# Revit family: QF_GIORIK_MR4_MR42_MDR42
name_source: partatom
category: Specialty Equipment
revit_build: Autodesk Revit 2014 (Build: 20140709_2115(x64)
units: mm (PartAtom-declared; Revit-internal decimal feet)

## types (6) — shared parameters
Apparent Power = 6300 VA
Assembly Code = E1090320
Cold Water Connection Height = 56 mm  [stored 0.183727 ft]
Cold Water Size = 1"
Cold Water Temperature Recommended = 0 °C
Cycle = 50 Hz
FL Amps = 0 A
HP = 0
Indirect Waste Connection Height = 25 mm  [stored 0.082021 ft]
Indirect Waste Flow = 0.0 L/s
Indirect Waste Size = 1"
Manufacturer = GIORIK
Max Overcurrent Protection = 20 A
Min Ckt Ampacity = 0 A
Phase = 3
URL = www.giorik.com
Volts = 400 V
Waste Water Discharge Temperature = 0 °C
Watts = 6300 W
Weight in Pounds = 138.891

## per-type parameters (varying)
| type | Description | Digital control | Electromechanical control with humidifier and two fan speed | Electromechanical control without humidifier |
| MR42 | CONVECTION OVEN 4 GN 1/1 - 600X400 ELECTROMECHANICAL CONTROL WITH HUMIDIFIER AND TWO FAN SPEED | No | Yes | No |
| MDR42 | CONVECTION OVEN 4 GN 1/1 - 600X400 PROGRAMMABLE DIGITAL CONTROL | Yes | No | No |
| MR4 | CONVECTION OVEN 4 GN 1/1 - 600X400 ELECTROMECHANICAL CONTROL WITHOUT HUMIDIFIER | No | No | Yes |
| MR4X | CONVECTION OVEN EXTRA POWERED 4 GN 1/1 - 600X400 ELECTROMECHANICAL CONTROL WITHOUT HUMIDIFIER | No | No | Yes |
| MR42X | CONVECTION OVEN EXTRA POWERED 4 GN 1/1 - 600X400 ELECTROMECHANICAL CONTROL WITH HUMIDIFIER AND TWO FAN SPEED | No | Yes | No |
| MDR42X | CONVECTION OVEN EXTRA POWERED 4 GN 1/1 - 600X400 PROGRAMMABLE DIGITAL CONTROL | Yes | No | No |

note: column(s) folded — value = type name in every type: Model

note: [stored X ft] marks values corroborated as IEEE doubles in the binary element streams (Revit-internal decimal feet)

## geometry (parser evidence)
native form markers: Blend x2, Sweep x1
no freeform markers — native parametric forms only
